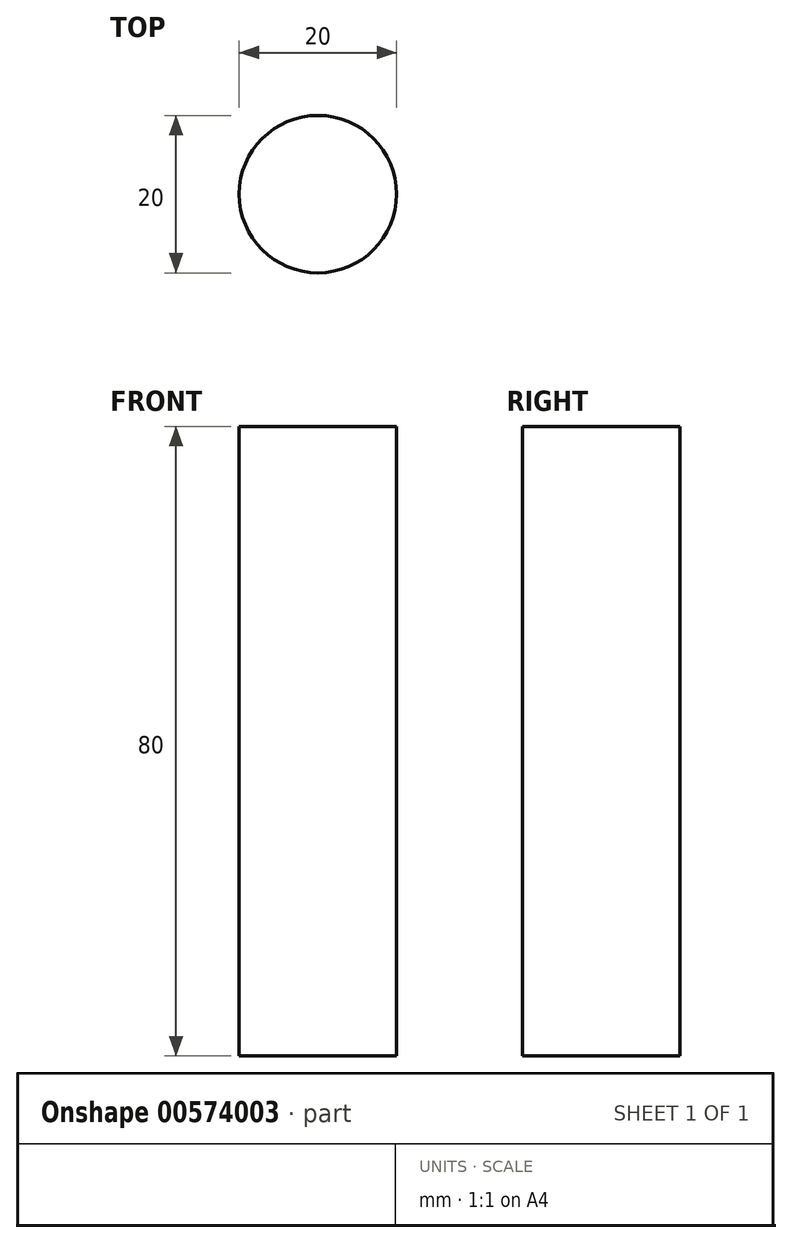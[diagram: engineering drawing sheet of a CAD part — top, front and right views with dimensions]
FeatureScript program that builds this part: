
annotation { "Feature Type Name" : "Feature", "Feature Type Description" : "" }
export const myFeature = defineFeature(function(context is Context, id is Id, definition is map)
    precondition{}
    {
        {
            var Q0;
            Q0=qCreatedBy(makeId("Top.planeOp"),FACE);
            var sketch = newSketch(context, id + "F0", { "sketchPlane" : qUnion([Q0])});
            skCircle(sketch, "E0", {"center": v(0, 0) * mm, "radius": 10 * mm});
            skSolve(sketch);
        }
        {
            var Q0;
            Q0 = qSketchRegion(id + "F0", true);
            extrude(context, id + "F1", {"entities" : qUnion([Q0]), "depth" : 80 * mm, "offsetDistance" : 25 * mm});
        }
    });
